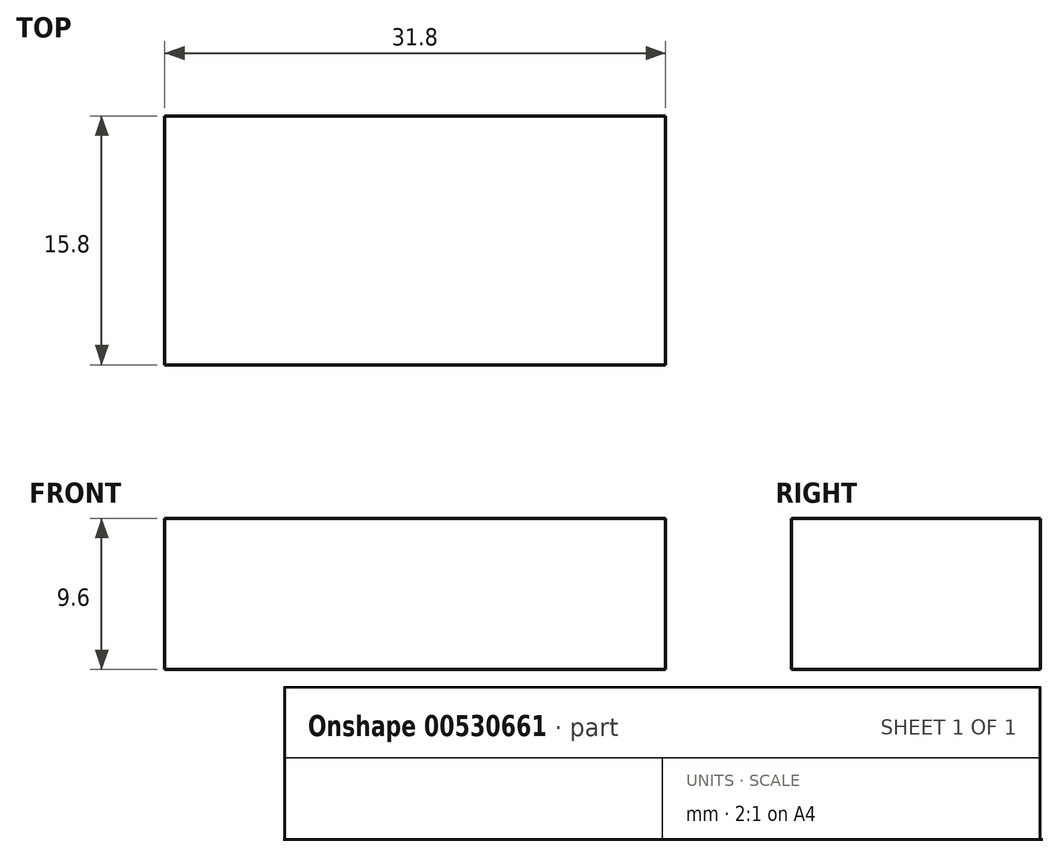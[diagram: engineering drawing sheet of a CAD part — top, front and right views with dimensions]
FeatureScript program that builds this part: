
annotation { "Feature Type Name" : "Feature", "Feature Type Description" : "" }
export const myFeature = defineFeature(function(context is Context, id is Id, definition is map)
    precondition{}
    {
        {
            var Q0;
            Q0=qCreatedBy(makeId("Front.planeOp"),FACE);
            var sketch = newSketch(context, id + "F0", { "sketchPlane" : qUnion([Q0])});
            skLineSegment(sketch, "E0", {"start": v(0, 0) * mm, "end": v(15.9, 0) * mm});
            skLineSegment(sketch, "E1.MirrorCS", {"start": v(0, 0) * mm, "end": v(-15.9, 0) * mm});
            skLineSegment(sketch, "E2", {"start": v(-15.9, 0) * mm, "end": v(-15.9, 9.6) * mm});
            skLineSegment(sketch, "E3.MirrorCS", {"start": v(15.9, 0) * mm, "end": v(15.9, 9.6) * mm});
            skLineSegment(sketch, "E4", {"start": v(-15.9, 9.6) * mm, "end": v(15.9, 9.6) * mm});
            skSolve(sketch);
        }
        {
            var Q0;
            Q0 = qSketchRegion(id + "F0", true);
            extrude(context, id + "F1", {"entities" : qUnion([Q0]), "endBound" : BoundingType.SYMMETRIC, "depth" : 15.8 * mm, "offsetDistance" : 25 * mm});
        }
    });
